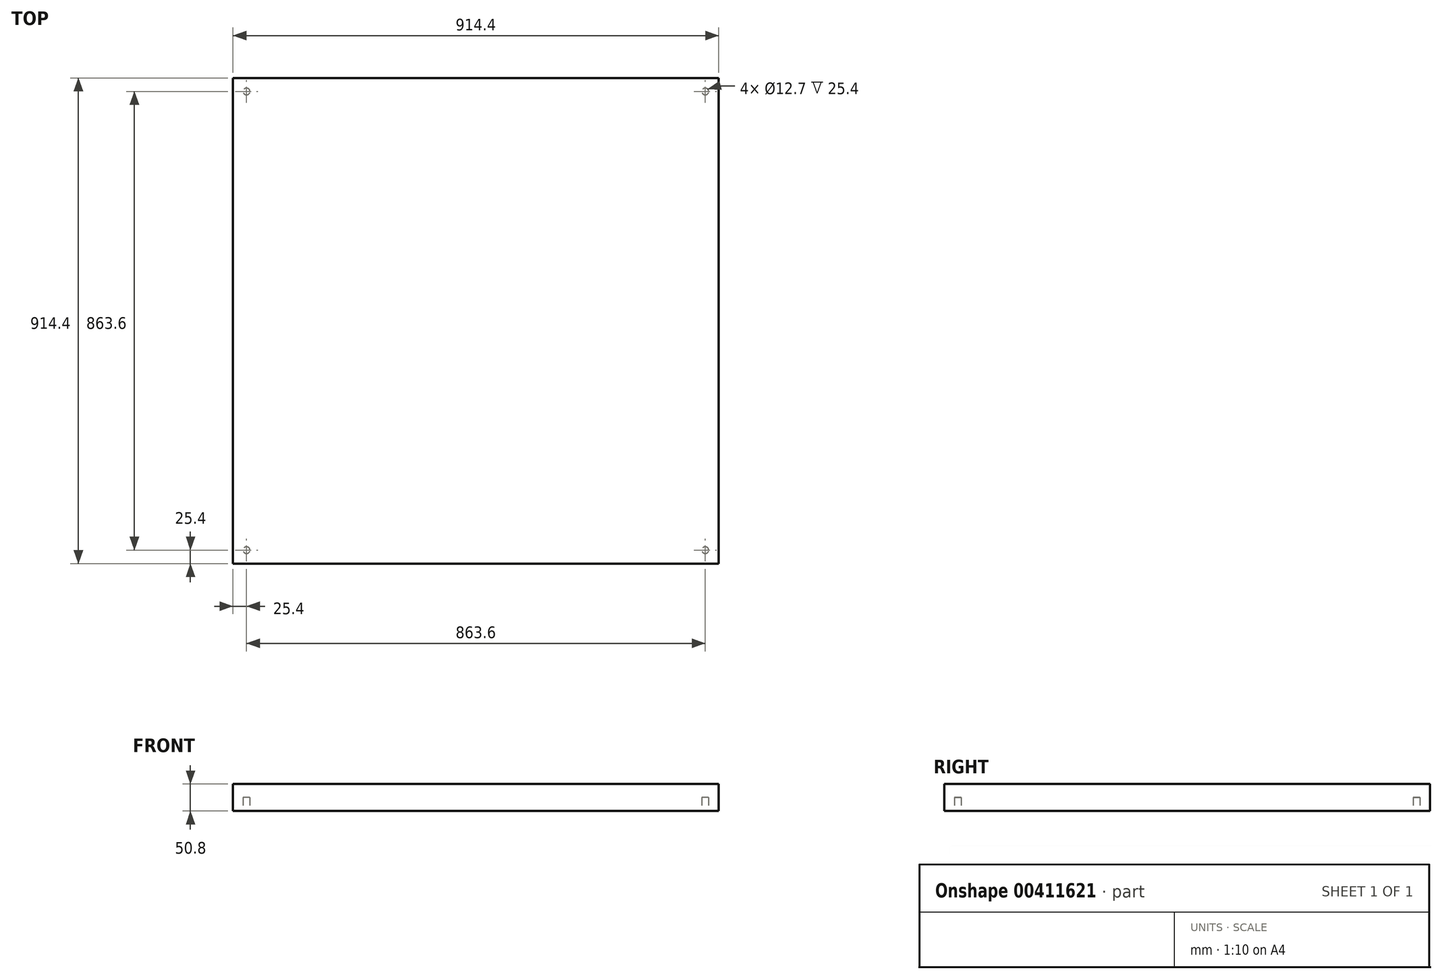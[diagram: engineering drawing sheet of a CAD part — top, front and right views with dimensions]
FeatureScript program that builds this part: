
annotation { "Feature Type Name" : "Feature", "Feature Type Description" : "" }
export const myFeature = defineFeature(function(context is Context, id is Id, definition is map)
    precondition{}
    {
        {
            var Q0;
            Q0=qCreatedBy(makeId("Top.planeOp"),FACE);
            var sketch = newSketch(context, id + "F0", { "sketchPlane" : qUnion([Q0])});
            skLineSegment(sketch, "E0.bottom", {"start": v(-457.2, 457.2) * mm, "end": v(457.2, 457.2) * mm});
            skLineSegment(sketch, "E0.top", {"start": v(-457.2, -457.2) * mm, "end": v(457.2, -457.2) * mm});
            skLineSegment(sketch, "E0.left", {"start": v(-457.2, 457.2) * mm, "end": v(-457.2, -457.2) * mm});
            skLineSegment(sketch, "E0.right", {"start": v(457.2, 457.2) * mm, "end": v(457.2, -457.2) * mm});
            skSolve(sketch);
        }
        {
            var Q0;
            Q0 = qSketchRegion(id + "F0", true);
            extrude(context, id + "F1", {"entities" : qUnion([Q0]), "depth" : 50.8 * mm});
        }
        {
            var Q0;
            Q0=qCreatedBy(makeId("Top.planeOp"),FACE);
            var sketch = newSketch(context, id + "F2", { "sketchPlane" : qUnion([Q0])});
            skLineSegment(sketch, "E1.0", {"start": v(-431.8, -431.8) * mm, "end": v(431.8, -431.8) * mm, "construction": true});
            skLineSegment(sketch, "E1.1", {"start": v(-431.8, 431.8) * mm, "end": v(-431.8, -431.8) * mm, "construction": true});
            skLineSegment(sketch, "E1.2", {"start": v(-431.8, 431.8) * mm, "end": v(431.8, 431.8) * mm, "construction": true});
            skLineSegment(sketch, "E1.3", {"start": v(431.8, 431.8) * mm, "end": v(431.8, -431.8) * mm, "construction": true});
            skCircle(sketch, "E2", {"center": v(-431.8, -431.8) * mm, "radius": 6.35 * mm});
            skCircle(sketch, "E3", {"center": v(431.8, -431.8) * mm, "radius": 6.35 * mm});
            skCircle(sketch, "E4", {"center": v(431.8, 431.8) * mm, "radius": 6.35 * mm});
            skCircle(sketch, "E5", {"center": v(-431.8, 431.8) * mm, "radius": 6.35 * mm});
            skSolve(sketch);
        }
        {
            var Q0;
            Q0 = qSketchRegion(id + "F2", true);
            extrude(context, id + "F3", {"entities" : qUnion([Q0]), "operationType" : NewBodyOperationType.REMOVE, "depth" : 25.4 * mm});
        }
    });
